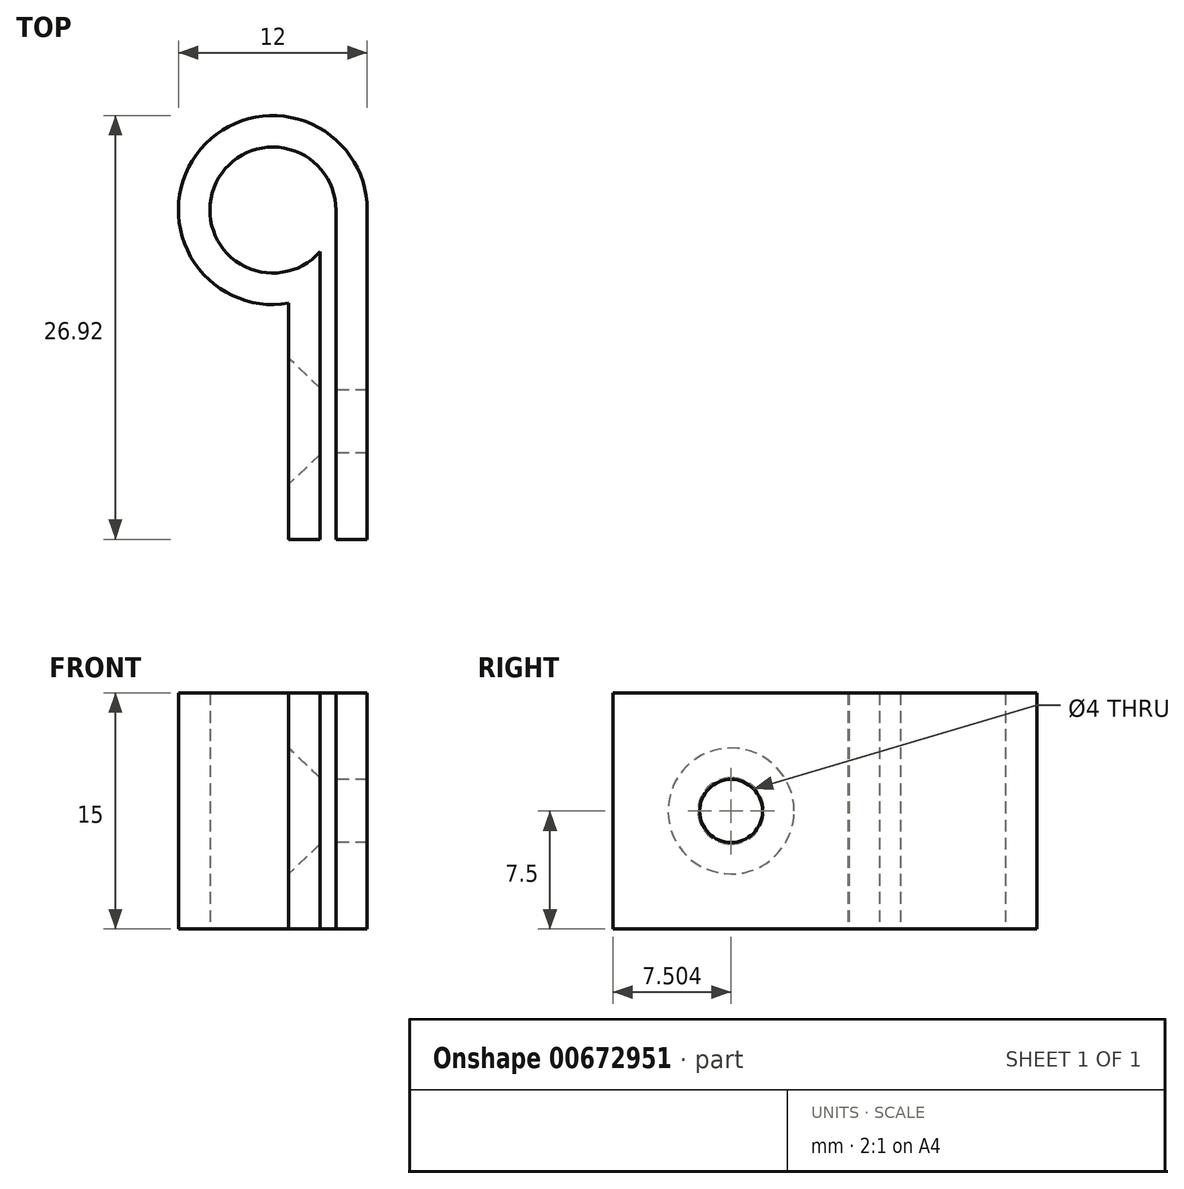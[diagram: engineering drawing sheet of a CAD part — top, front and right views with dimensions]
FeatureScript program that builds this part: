
annotation { "Feature Type Name" : "Feature", "Feature Type Description" : "" }
export const myFeature = defineFeature(function(context is Context, id is Id, definition is map)
    precondition{}
    {
        {
            var Q0;
            Q0=qCreatedBy(makeId("Top.planeOp"),FACE);
            var sketch = newSketch(context, id + "F0", { "sketchPlane" : qUnion([Q0])});
            skArc(sketch, "E0", {"start": v(4, 0) * mm, "mid": v(-3.74, 1.41) * mm, "end": v(3, -2.65) * mm});
            skArc(sketch, "E1", {"start": v(6, 0) * mm, "mid": v(-4.58, 3.87) * mm, "end": v(1, -5.92) * mm});
            skLineSegment(sketch, "E2", {"start": v(6, 0) * mm, "end": v(6, -20.92) * mm});
            skLineSegment(sketch, "E3", {"start": v(6, -20.92) * mm, "end": v(4, -20.92) * mm});
            skLineSegment(sketch, "E4", {"start": v(4, -20.92) * mm, "end": v(4, 0) * mm});
            skLineSegment(sketch, "E5", {"start": v(3, -2.65) * mm, "end": v(3, -20.92) * mm});
            skLineSegment(sketch, "E6", {"start": v(3, -20.92) * mm, "end": v(1, -20.92) * mm});
            skLineSegment(sketch, "E7", {"start": v(1, -20.92) * mm, "end": v(1, -5.92) * mm});
            skSolve(sketch);
        }
        {
            var Q0;
            Q0=makeQuery(id+"F0.imprint","IMPRINT",FACE,{"disambiguationData":[TD([[makeQuery(id+"F0.imprint","IMPRINT",EDGE,{"derivedFrom":sQuery(id+"F0.wireOp",EDGE,"E0")}),-1.0]])]});
            extrude(context, id + "F1", {"entities" : qUnion([Q0]), "depth" : 15 * mm, "offsetDistance" : 25 * mm});
        }
        {
            var Q0;
            Q0=makeQuery(id+"F1.opExtrude","SWEPT_FACE",FACE,{"disambiguationData":[OSD([sQuery(id+"F0.wireOp",EDGE,"E7")])]});
            var sketch = newSketch(context, id + "F2", { "sketchPlane" : qUnion([Q0])});
            skLineSegment(sketch, "E8", {"start": v(20.92, 15) * mm, "end": v(5.92, 0) * mm, "construction": true});
            skCircle(sketch, "E9", {"center": v(13.42, 7.5) * mm, "radius": 2 * mm});
            skSolve(sketch);
        }
        {
            var Q0;
            Q0 = qSketchRegion(id + "F2", true);
            var Q1;
            Q1=makeQuery(id+"F1.opExtrude","SWEPT_FACE",FACE,{"disambiguationData":[OSD([sQuery(id+"F0.wireOp",EDGE,"E2")])]});
            extrude(context, id + "F3", {"entities" : qUnion([Q0]), "operationType" : NewBodyOperationType.REMOVE, "endBound" : BoundingType.UP_TO_SURFACE, "oppositeDirection" : true, "depth" : 25 * mm, "endBoundEntityFace" : qUnion([Q1]), "offsetDistance" : 25 * mm});
        }
        {
            var Q0;
            Q0=makeQuery(id+"F1.opExtrude","SWEPT_FACE",FACE,{"disambiguationData":[OSD([sQuery(id+"F0.wireOp",EDGE,"E7")])]});
            var sketch = newSketch(context, id + "F4", { "sketchPlane" : qUnion([Q0])});
            skCircle(sketch, "E10", {"center": v(13.42, 7.5) * mm, "radius": 4 * mm});
            skSolve(sketch);
        }
        {
            var Q0;
            Q0=makeQuery(id+"F1.opExtrude","SWEPT_FACE",FACE,{"disambiguationData":[OSD([sQuery(id+"F0.wireOp",EDGE,"E5")])]});
            var sketch = newSketch(context, id + "F5", { "sketchPlane" : qUnion([Q0])});
            skCircle(sketch, "E11", {"center": v(-13.42, 7.5) * mm, "radius": 2.1 * mm});
            skSolve(sketch);
        }
        {
            var Q1;
            Q1 = qSketchRegion(id + "F4", true);
            var Q2;
            Q2 = qSketchRegion(id + "F5", true);
            loft(context, id + "F6", {"operationType" : NewBodyOperationType.REMOVE, "sheetProfilesArray" : [{ "sheetProfileEntities" : qUnion([Q1]) }, { "sheetProfileEntities" : qUnion([Q2]) }]});
        }
    });
